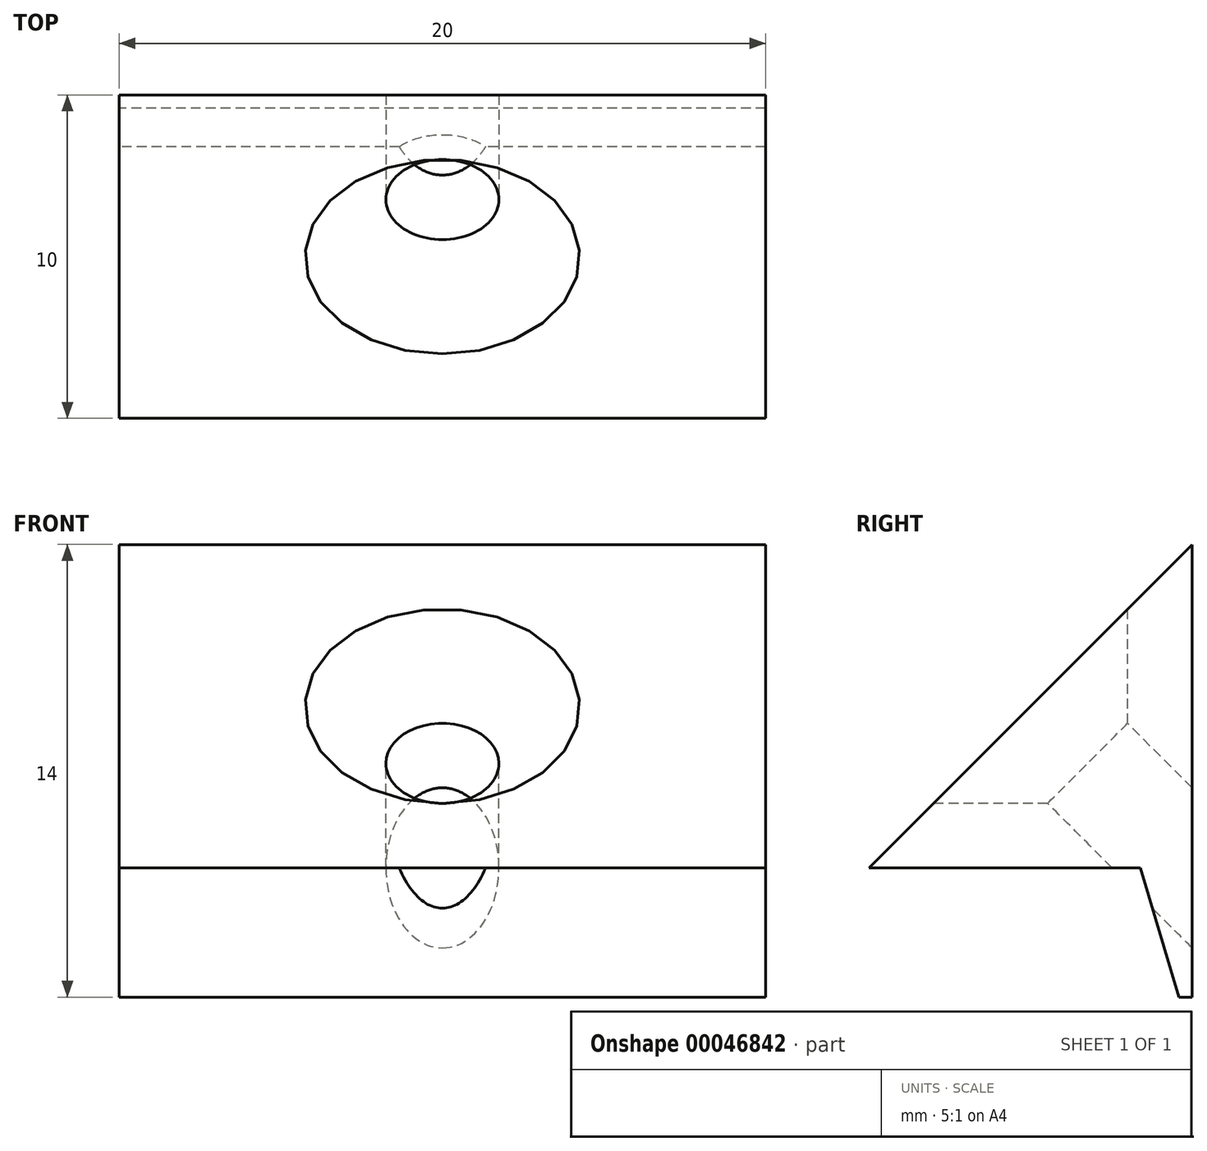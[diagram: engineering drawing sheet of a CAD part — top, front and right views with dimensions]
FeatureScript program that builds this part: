
annotation { "Feature Type Name" : "Feature", "Feature Type Description" : "" }
export const myFeature = defineFeature(function(context is Context, id is Id, definition is map)
    precondition{}
    {
        {
            var Q0;
            Q0=qCreatedBy(makeId("Right.planeOp"),FACE);
            var sketch = newSketch(context, id + "F0", { "sketchPlane" : qUnion([Q0])});
            skLineSegment(sketch, "E0", {"start": v(-27.41, -10.4) * mm, "end": v(-17.41, -10.4) * mm});
            skLineSegment(sketch, "E1", {"start": v(-17.41, -10.4) * mm, "end": v(-17.41, -0.4) * mm});
            skLineSegment(sketch, "E2", {"start": v(-17.41, -0.4) * mm, "end": v(-27.41, -10.4) * mm});
            skLineSegment(sketch, "E3", {"start": v(-17.41, -10.4) * mm, "end": v(-17.41, -14.4) * mm});
            skLineSegment(sketch, "E4", {"start": v(-17.81, -14.4) * mm, "end": v(-19.01, -10.4) * mm});
            skLineSegment(sketch, "E5", {"start": v(-17.41, -14.4) * mm, "end": v(-17.81, -14.4) * mm});
            skSolve(sketch);
        }
        {
            var Q0;
            Q0 = qSketchRegion(id + "F0", true);
            extrude(context, id + "F1", {"entities" : qUnion([Q0]), "depth" : 20 * mm});
        }
        {
            var Q0;
            Q0=makeQuery(id+"F1.opExtrude","SWEPT_FACE",FACE,{"disambiguationData":[OSD([sQuery(id+"F0.wireOp",EDGE,"E2")])]});
            var sketch = newSketch(context, id + "F2", { "sketchPlane" : qUnion([Q0])});
            skLineSegment(sketch, "E6.rect.bottom", {"start": v(20, -26.74) * mm, "end": v(0, -26.74) * mm, "construction": true});
            skLineSegment(sketch, "E6.rect.top", {"start": v(20, -12.6) * mm, "end": v(0, -12.6) * mm, "construction": true});
            skLineSegment(sketch, "E6.rect.left", {"start": v(20, -26.74) * mm, "end": v(20, -12.6) * mm, "construction": true});
            skLineSegment(sketch, "E6.rect.right", {"start": v(0, -26.74) * mm, "end": v(0, -12.6) * mm, "construction": true});
            skPoint(sketch, "E6.rect.middle", {"position": v(10, -19.67) * mm});
            skSolve(sketch);
        }
        {
            var Q0;
            Q0=sQuery(id+"F2.wireOp",VERTEX,"E6.rect.middle");
            var Q1;
            Q1=makeQuery(id+"F1.opExtrude","SWEPT_BODY",BODY,{"disambiguationData":[OSD([sQuery(id+"F0.wireOp",EDGE,"E0"),sQuery(id+"F0.wireOp",EDGE,"E1"),sQuery(id+"F0.wireOp",EDGE,"E2"),sQuery(id+"F0.wireOp",EDGE,"E3"),sQuery(id+"F0.wireOp",EDGE,"E4")])]});
            hole(context, id + "F3", {"style" : HoleStyle.C_SINK, "holeDiameter" : 3.5 * mm, "cSinkDiameter" : 8.5 * mm, "endStyle" : HoleEndStyle.THROUGH, "locations" : qUnion([Q0]), "scope" : qUnion([Q1]), "cSinkAngle" : 90 * degree, "majorDiameter" : 5 * mm, "tappedDepth" : 12 * mm, "tapClearance" : 3, "startFromSketch" : true});
        }
    });
